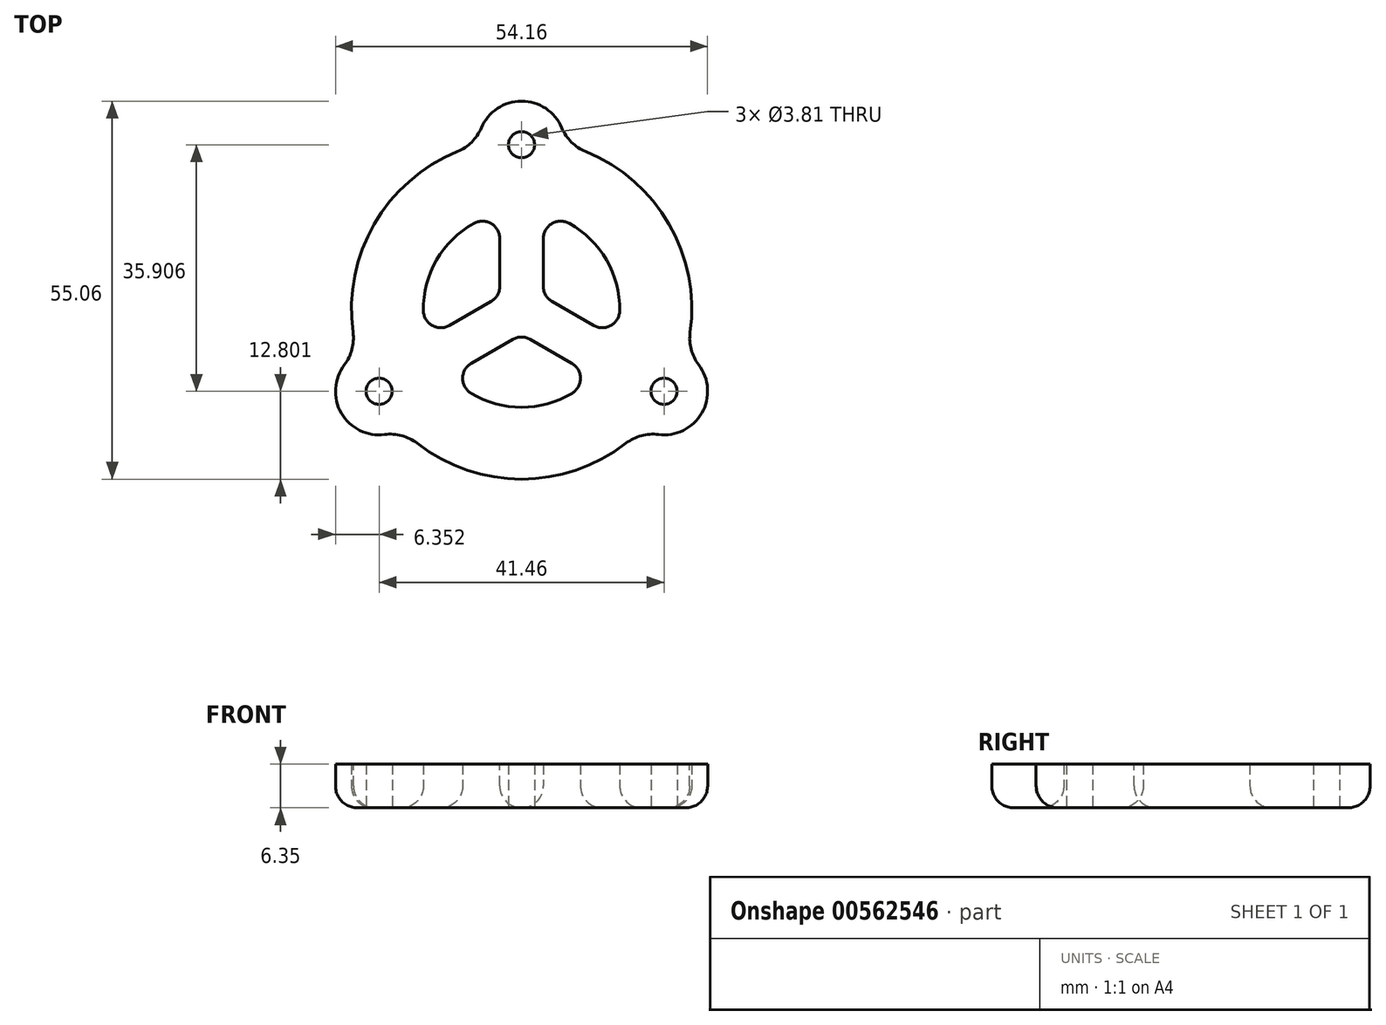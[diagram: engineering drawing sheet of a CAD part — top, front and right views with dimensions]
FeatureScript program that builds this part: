
annotation { "Feature Type Name" : "Feature", "Feature Type Description" : "" }
export const myFeature = defineFeature(function(context is Context, id is Id, definition is map)
    precondition{}
    {
        {
            var Q0;
            Q0=qCreatedBy(makeId("Top.planeOp"),FACE);
            var sketch = newSketch(context, id + "F0", { "sketchPlane" : qUnion([Q0])});
            skCircle(sketch, "E0", {"center": v(-1.59, 1.16) * mm, "radius": 14.29 * mm});
            skCircle(sketch, "E1", {"center": v(-1.59, 1.16) * mm, "radius": 24.77 * mm});
            skLineSegment(sketch, "E2", {"start": v(-1.59, 1.16) * mm, "end": v(-1.59, 43.93) * mm, "construction": true});
            skLineSegment(sketch, "E3", {"start": v(-1.59, 1.16) * mm, "end": v(-45.3, -24.08) * mm, "construction": true});
            skLineSegment(sketch, "E4", {"start": v(-1.59, 1.16) * mm, "end": v(44.64, -25.53) * mm, "construction": true});
            skLineSegment(sketch, "E5", {"start": v(-7.94, 3.32) * mm, "end": v(-7.94, 50.13) * mm, "construction": true});
            skLineSegment(sketch, "E6.MirrorCS", {"start": v(4.76, 3.32) * mm, "end": v(4.76, 50.13) * mm, "construction": true});
            skLineSegment(sketch, "E7", {"start": v(-12.82, 2) * mm, "end": v(-50.57, -19.8) * mm, "construction": true});
            skLineSegment(sketch, "E8.MirrorCS", {"start": v(-6.47, -9) * mm, "end": v(-44.22, -30.79) * mm, "construction": true});
            skLineSegment(sketch, "E9", {"start": v(-2.12, -5.87) * mm, "end": v(36.22, -28) * mm, "construction": true});
            skLineSegment(sketch, "E10.MirrorCS", {"start": v(4.23, 5.13) * mm, "end": v(42.57, -17) * mm, "construction": true});
            skArc(sketch, "E11", {"start": v(4.76, 25.1) * mm, "mid": v(-1.59, 31.45) * mm, "end": v(-7.94, 25.1) * mm});
            skArc(sketch, "E12", {"start": v(-25.5, -5.3) * mm, "mid": v(-27.82, -13.98) * mm, "end": v(-19.14, -16.3) * mm});
            skArc(sketch, "E13", {"start": v(15.97, -16.3) * mm, "mid": v(24.64, -13.98) * mm, "end": v(22.32, -5.3) * mm});
            skCircle(sketch, "E14", {"center": v(-1.59, 25.1) * mm, "radius": 1.9 * mm});
            skCircle(sketch, "E15", {"center": v(-22.32, -10.8) * mm, "radius": 1.9 * mm});
            skCircle(sketch, "E16", {"center": v(19.14, -10.8) * mm, "radius": 1.9 * mm});
            skCircle(sketch, "E17", {"center": v(-1.59, 1.16) * mm, "radius": 3.18 * mm, "construction": true});
            skLineSegment(sketch, "E18", {"start": v(-4.76, 1.16) * mm, "end": v(-4.76, 15.1) * mm});
            skLineSegment(sketch, "E19.MirrorCS", {"start": v(1.59, 1.16) * mm, "end": v(1.59, 15.1) * mm});
            skLineSegment(sketch, "E20", {"start": v(0, 3.9) * mm, "end": v(12.06, -3.06) * mm});
            skLineSegment(sketch, "E21.MirrorCS", {"start": v(-3.18, -1.59) * mm, "end": v(8.89, -8.55) * mm});
            skLineSegment(sketch, "E22", {"start": v(-15.24, -3.06) * mm, "end": v(-3.17, 3.9) * mm});
            skLineSegment(sketch, "E23.MirrorCS", {"start": v(-12.06, -8.55) * mm, "end": v(0, -1.59) * mm});
            skSolve(sketch);
        }
        {
            var Q0;
            {var subQ11=sQuery(id+"F0.wireOp",EDGE,"E0");var subQ15=makeQuery(id+"F0.imprint","INTERSECT",VERTEX,{"derivedFrom":[subQ11,sQuery(id+"F0.wireOp",EDGE,"E18")]});Q0=makeQuery(id+"F0.imprint","IMPRINT",FACE,{"disambiguationData":[TD([[makeQuery(id+"F0.imprint","IMPRINT",EDGE,{"disambiguationData":[TD([[subQ15,1.0]])],"derivedFrom":subQ11}),-1.0]])]});}
            var Q1;
            {var subQ1=sQuery(id+"F0.wireOp",EDGE,"E0");var subQ5=sQuery(id+"F0.wireOp",EDGE,"E18");var subQ6=makeQuery(id+"F0.imprint","INTERSECT",VERTEX,{"derivedFrom":[subQ1,subQ5]});Q1=makeQuery(id+"F0.imprint","IMPRINT",FACE,{"disambiguationData":[TD([[makeQuery(id+"F0.imprint","IMPRINT",EDGE,{"disambiguationData":[TD([[subQ6,1.0]])],"derivedFrom":subQ1}),1.0]])]});}
            var Q2;
            {var subQ0=sQuery(id+"F0.wireOp",EDGE,"E12");Q2=makeQuery(id+"F0.imprint","IMPRINT",FACE,{"disambiguationData":[TD([[makeQuery(id+"F0.imprint","IMPRINT",EDGE,{"derivedFrom":subQ0}),1.0]])]});}
            var Q3;
            {var subQ0=sQuery(id+"F0.wireOp",EDGE,"E13");Q3=makeQuery(id+"F0.imprint","IMPRINT",FACE,{"disambiguationData":[TD([[makeQuery(id+"F0.imprint","IMPRINT",EDGE,{"derivedFrom":subQ0}),1.0]])]});}
            var Q4;
            {var subQ0=sQuery(id+"F0.wireOp",EDGE,"E11");Q4=makeQuery(id+"F0.imprint","IMPRINT",FACE,{"disambiguationData":[TD([[makeQuery(id+"F0.imprint","IMPRINT",EDGE,{"derivedFrom":subQ0}),1.0]])]});}
            extrude(context, id + "F1", {"entities" : qUnion([Q0, Q1, Q2, Q3, Q4]), "depth" : 6.35 * mm, "offsetDistance" : 25.4 * mm});
        }
        {
            var Q0;
            {var subQ0=sQuery(id+"F0.wireOp",EDGE,"E13");var subQ1=sQuery(id+"F0.wireOp",EDGE,"E1");Q0=makeQuery(id+"F1.opExtrude","SWEPT_EDGE",EDGE,{"disambiguationData":[OSD([subQ1,subQ0]),TDD([makeQuery(id+"F0.imprint","INTERSECT",VERTEX,{"disambiguationData":[OD(0.0)],"derivedFrom":[subQ1,subQ0]})])]});}
            var Q1;
            {var subQ0=sQuery(id+"F0.wireOp",EDGE,"E13");var subQ1=sQuery(id+"F0.wireOp",EDGE,"E1");Q1=makeQuery(id+"F1.opExtrude","SWEPT_EDGE",EDGE,{"disambiguationData":[OSD([subQ1,subQ0]),TDD([makeQuery(id+"F0.imprint","INTERSECT",VERTEX,{"disambiguationData":[OD(1.0)],"derivedFrom":[subQ1,subQ0]})])]});}
            var Q2;
            {var subQ0=sQuery(id+"F0.wireOp",EDGE,"E11");var subQ1=sQuery(id+"F0.wireOp",EDGE,"E1");Q2=makeQuery(id+"F1.opExtrude","SWEPT_EDGE",EDGE,{"disambiguationData":[OSD([subQ1,subQ0]),TDD([makeQuery(id+"F0.imprint","INTERSECT",VERTEX,{"disambiguationData":[OD(0.0)],"derivedFrom":[subQ1,subQ0]})])]});}
            var Q3;
            {var subQ0=sQuery(id+"F0.wireOp",EDGE,"E11");var subQ1=sQuery(id+"F0.wireOp",EDGE,"E1");Q3=makeQuery(id+"F1.opExtrude","SWEPT_EDGE",EDGE,{"disambiguationData":[OSD([subQ1,subQ0]),TDD([makeQuery(id+"F0.imprint","INTERSECT",VERTEX,{"disambiguationData":[OD(1.0)],"derivedFrom":[subQ1,subQ0]})])]});}
            var Q4;
            {var subQ0=sQuery(id+"F0.wireOp",EDGE,"E12");var subQ1=sQuery(id+"F0.wireOp",EDGE,"E1");Q4=makeQuery(id+"F1.opExtrude","SWEPT_EDGE",EDGE,{"disambiguationData":[OSD([subQ1,subQ0]),TDD([makeQuery(id+"F0.imprint","INTERSECT",VERTEX,{"disambiguationData":[OD(0.0)],"derivedFrom":[subQ1,subQ0]})])]});}
            var Q5;
            {var subQ0=sQuery(id+"F0.wireOp",EDGE,"E12");var subQ1=sQuery(id+"F0.wireOp",EDGE,"E1");Q5=makeQuery(id+"F1.opExtrude","SWEPT_EDGE",EDGE,{"disambiguationData":[OSD([subQ1,subQ0]),TDD([makeQuery(id+"F0.imprint","INTERSECT",VERTEX,{"disambiguationData":[OD(1.0)],"derivedFrom":[subQ1,subQ0]})])]});}
            fillet(context, id + "F2", {"entities" : qUnion([Q0, Q1, Q2, Q3, Q4, Q5]), "radius" : 6.35 * mm, "tangentPropagation" : true, "allowEdgeOverflow" : false});
        }
        {
            var Q0;
            Q0=makeQuery(id+"F1.opExtrude","SWEPT_EDGE",EDGE,{"disambiguationData":[OSD([sQuery(id+"F0.wireOp",EDGE,"E0"),sQuery(id+"F0.wireOp",EDGE,"E22")])]});
            var Q1;
            Q1=makeQuery(id+"F1.opExtrude","SWEPT_EDGE",EDGE,{"disambiguationData":[OSD([sQuery(id+"F0.wireOp",EDGE,"E0"),sQuery(id+"F0.wireOp",EDGE,"E23.MirrorCS")])]});
            var Q2;
            Q2=makeQuery(id+"F1.opExtrude","SWEPT_EDGE",EDGE,{"disambiguationData":[OSD([sQuery(id+"F0.wireOp",EDGE,"E0"),sQuery(id+"F0.wireOp",EDGE,"E21.MirrorCS")])]});
            var Q3;
            Q3=makeQuery(id+"F1.opExtrude","SWEPT_EDGE",EDGE,{"disambiguationData":[OSD([sQuery(id+"F0.wireOp",EDGE,"E21.MirrorCS"),sQuery(id+"F0.wireOp",EDGE,"E23.MirrorCS")])]});
            var Q4;
            Q4=makeQuery(id+"F1.opExtrude","SWEPT_EDGE",EDGE,{"disambiguationData":[OSD([sQuery(id+"F0.wireOp",EDGE,"E18"),sQuery(id+"F0.wireOp",EDGE,"E22")])]});
            var Q5;
            Q5=makeQuery(id+"F1.opExtrude","SWEPT_EDGE",EDGE,{"disambiguationData":[OSD([sQuery(id+"F0.wireOp",EDGE,"E0"),sQuery(id+"F0.wireOp",EDGE,"E18")])]});
            var Q6;
            Q6=makeQuery(id+"F1.opExtrude","SWEPT_EDGE",EDGE,{"disambiguationData":[OSD([sQuery(id+"F0.wireOp",EDGE,"E19.MirrorCS"),sQuery(id+"F0.wireOp",EDGE,"E20")])]});
            var Q7;
            Q7=makeQuery(id+"F1.opExtrude","SWEPT_EDGE",EDGE,{"disambiguationData":[OSD([sQuery(id+"F0.wireOp",EDGE,"E0"),sQuery(id+"F0.wireOp",EDGE,"E19.MirrorCS")])]});
            var Q8;
            Q8=makeQuery(id+"F1.opExtrude","SWEPT_EDGE",EDGE,{"disambiguationData":[OSD([sQuery(id+"F0.wireOp",EDGE,"E0"),sQuery(id+"F0.wireOp",EDGE,"E20")])]});
            fillet(context, id + "F3", {"entities" : qUnion([Q0, Q1, Q2, Q3, Q4, Q5, Q6, Q7, Q8]), "radius" : 2.54 * mm, "tangentPropagation" : true, "allowEdgeOverflow" : false});
        }
        {
            var Q0;
            {var subQ0=sQuery(id+"F0.wireOp",EDGE,"E0");Q0=makeQuery(id+"F1.opExtrude","CAP_EDGE",EDGE,{"disambiguationData":[OSD([subQ0]),TDD([makeQuery(id+"F0.imprint","IMPRINT",EDGE,{"disambiguationData":[TD([[makeQuery(id+"F0.imprint","INTERSECT",VERTEX,{"derivedFrom":[subQ0,sQuery(id+"F0.wireOp",EDGE,"E21.MirrorCS")]}),1.0]])],"derivedFrom":subQ0})])],"isStart":true});}
            var Q1;
            {var subQ0=sQuery(id+"F0.wireOp",EDGE,"E0");Q1=makeQuery(id+"F1.opExtrude","CAP_EDGE",EDGE,{"disambiguationData":[OSD([subQ0]),TDD([makeQuery(id+"F0.imprint","IMPRINT",EDGE,{"disambiguationData":[TD([[makeQuery(id+"F0.imprint","INTERSECT",VERTEX,{"derivedFrom":[subQ0,sQuery(id+"F0.wireOp",EDGE,"E19.MirrorCS")]}),1.0]])],"derivedFrom":subQ0})])],"isStart":true});}
            var Q2;
            {var subQ0=sQuery(id+"F0.wireOp",EDGE,"E0");Q2=makeQuery(id+"F1.opExtrude","CAP_EDGE",EDGE,{"disambiguationData":[OSD([subQ0]),TDD([makeQuery(id+"F0.imprint","IMPRINT",EDGE,{"disambiguationData":[TD([[makeQuery(id+"F0.imprint","INTERSECT",VERTEX,{"derivedFrom":[subQ0,sQuery(id+"F0.wireOp",EDGE,"E18")]}),-1.0]])],"derivedFrom":subQ0})])],"isStart":true});}
            var Q3;
            {var subQ0=sQuery(id+"F0.wireOp",EDGE,"E1");Q3=makeQuery(id+"F1.opExtrude","CAP_EDGE",EDGE,{"disambiguationData":[OSD([subQ0]),TDD([makeQuery(id+"F0.imprint","IMPRINT",EDGE,{"disambiguationData":[TD([[makeQuery(id+"F0.imprint","INTERSECT",VERTEX,{"disambiguationData":[OD(1.0)],"derivedFrom":[subQ0,sQuery(id+"F0.wireOp",EDGE,"E12")]}),-1.0]])],"derivedFrom":subQ0})])],"isStart":true});}
            fillet(context, id + "F4", {"entities" : qUnion([Q0, Q1, Q2, Q3]), "radius" : 3.17 * mm, "tangentPropagation" : true, "allowEdgeOverflow" : false});
        }
    });
